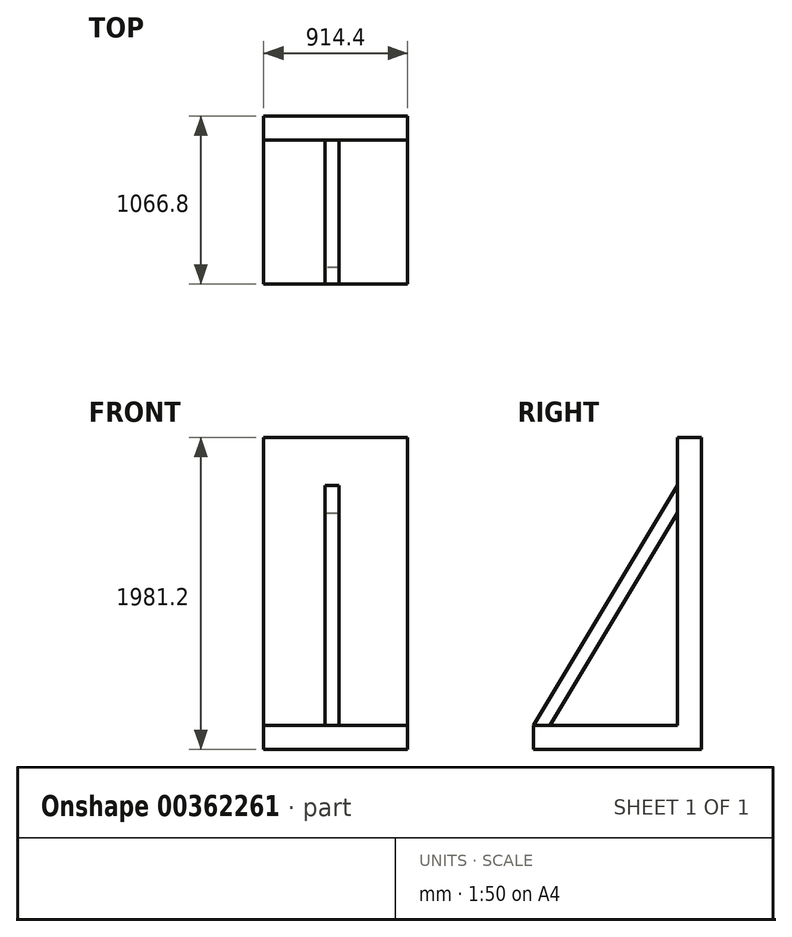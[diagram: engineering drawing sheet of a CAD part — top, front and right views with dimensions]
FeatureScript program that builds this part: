
annotation { "Feature Type Name" : "Feature", "Feature Type Description" : "" }
export const myFeature = defineFeature(function(context is Context, id is Id, definition is map)
    precondition{}
    {
        {
            var Q0;
            Q0=qCreatedBy(makeId("Front.planeOp"),FACE);
            var sketch = newSketch(context, id + "F0", { "sketchPlane" : qUnion([Q0])});
            skLineSegment(sketch, "E0.bottom", {"start": v(0, 0) * mm, "end": v(-914.4, 0) * mm});
            skLineSegment(sketch, "E0.top", {"start": v(0, 1828.8) * mm, "end": v(-914.4, 1828.8) * mm});
            skLineSegment(sketch, "E0.left", {"start": v(0, 0) * mm, "end": v(0, 1828.8) * mm});
            skLineSegment(sketch, "E0.right", {"start": v(-914.4, 0) * mm, "end": v(-914.4, 1828.8) * mm});
            skSolve(sketch);
        }
        {
            var Q0;
            Q0 = qSketchRegion(id + "F0", true);
            extrude(context, id + "F1", {"entities" : qUnion([Q0]), "depth" : 152.4 * mm});
        }
        {
            var Q0;
            Q0=qCreatedBy(makeId("Top.planeOp"),FACE);
            var sketch = newSketch(context, id + "F2", { "sketchPlane" : qUnion([Q0])});
            skLineSegment(sketch, "E1.0.0", {"start": v(0, 0) * mm, "end": v(-914.4, 0) * mm});
            skLineSegment(sketch, "E1.0.1", {"start": v(-914.4, 0) * mm, "end": v(-914.4, -152.4) * mm});
            skLineSegment(sketch, "E1.0.2", {"start": v(-914.4, -152.4) * mm, "end": v(0, -152.4) * mm});
            skLineSegment(sketch, "E1.0.3", {"start": v(0, -152.4) * mm, "end": v(0, 0) * mm});
            skLineSegment(sketch, "E2.top", {"start": v(-914.4, -1066.8) * mm, "end": v(0, -1066.8) * mm});
            skLineSegment(sketch, "E2.left", {"start": v(-914.4, -152.4) * mm, "end": v(-914.4, -1066.8) * mm});
            skLineSegment(sketch, "E2.right", {"start": v(0, -152.4) * mm, "end": v(0, -1066.8) * mm});
            skSolve(sketch);
        }
        {
            var Q0;
            Q0 = qSketchRegion(id + "F2", true);
            extrude(context, id + "F3", {"entities" : qUnion([Q0]), "operationType" : NewBodyOperationType.ADD, "oppositeDirection" : true, "depth" : 152.4 * mm});
        }
        {
            var Q0;
            Q0=makeQuery(id+"F3.opExtrude","CAP_FACE",FACE,{"disambiguationData":[OSD([sQuery(id+"F2.wireOp",EDGE,"E1.0.0"),sQuery(id+"F2.wireOp",EDGE,"E1.0.1"),sQuery(id+"F2.wireOp",EDGE,"E1.0.3"),sQuery(id+"F2.wireOp",EDGE,"E2.top"),sQuery(id+"F2.wireOp",EDGE,"E2.left"),sQuery(id+"F2.wireOp",EDGE,"E2.right")])],"isStart":true});
            var sketch = newSketch(context, id + "F4", { "sketchPlane" : qUnion([Q0])});
            skLineSegment(sketch, "E3.bottom", {"start": v(-435.57, -1066.8) * mm, "end": v(-524.47, -1066.8) * mm});
            skLineSegment(sketch, "E3.top", {"start": v(-435.57, -977.9) * mm, "end": v(-524.47, -977.9) * mm});
            skLineSegment(sketch, "E3.left", {"start": v(-435.57, -1066.8) * mm, "end": v(-435.57, -977.9) * mm});
            skLineSegment(sketch, "E3.right", {"start": v(-524.47, -1066.8) * mm, "end": v(-524.47, -977.9) * mm});
            skSolve(sketch);
        }
        {
            var Q0;
            Q0=makeQuery(id+"F1.opExtrude","CAP_FACE",FACE,{"disambiguationData":[OSD([sQuery(id+"F0.wireOp",EDGE,"E0.bottom"),sQuery(id+"F0.wireOp",EDGE,"E0.top"),sQuery(id+"F0.wireOp",EDGE,"E0.left"),sQuery(id+"F0.wireOp",EDGE,"E0.right")])],"isStart":false});
            var sketch = newSketch(context, id + "F5", { "sketchPlane" : qUnion([Q0])});
            skLineSegment(sketch, "E4", {"start": v(-457.2, 1828.8) * mm, "end": v(-457.2, 1524) * mm});
            skSolve(sketch);
        }
        {
            var Q0;
            Q0=sQuery(id+"F4.wireOp",VERTEX,"E3.right.start");
            var Q1;
            Q1=sQuery(id+"F4.wireOp",VERTEX,"E3.left.start");
            var Q2;
            Q2=sQuery(id+"F5.wireOp",VERTEX,"E4.end");
            cPlane(context, id + "F6", {"entities" : qUnion([Q0, Q1, Q2]), "cplaneType" : CPlaneType.THREE_POINT, "offset" : 25.4 * mm, "width" : 152.4 * mm, "height" : 152.4 * mm});
        }
        {
            var Q0;
            Q0=qCreatedBy(id+"F6.planeOp",FACE);
            var sketch = newSketch(context, id + "F7", { "sketchPlane" : qUnion([Q0])});
            skLineSegment(sketch, "E5.0.1", {"start": v(524.47, -548.86) * mm, "end": v(435.57, -548.86) * mm});
            skPoint(sketch, "E6.0", {"position": v(457.2, 1228.41) * mm});
            skLineSegment(sketch, "E6.1.0", {"start": v(914.4, -78.4) * mm, "end": v(0, -78.4) * mm});
            skLineSegment(sketch, "E6.1.1", {"start": v(0, -78.4) * mm, "end": v(0, 1489.77) * mm});
            skLineSegment(sketch, "E6.1.2", {"start": v(0, 1489.77) * mm, "end": v(457.2, 1489.77) * mm});
            skLineSegment(sketch, "E6.1.3", {"start": v(457.2, 1489.77) * mm, "end": v(914.4, 1489.77) * mm});
            skLineSegment(sketch, "E6.1.4", {"start": v(914.4, 1489.77) * mm, "end": v(914.4, -78.4) * mm});
            skLineSegment(sketch, "E7", {"start": v(524.47, -503.13) * mm, "end": v(524.47, 1228.41) * mm});
            skLineSegment(sketch, "E8", {"start": v(435.57, -503.13) * mm, "end": v(435.57, 1228.41) * mm});
            skLineSegment(sketch, "E9", {"start": v(435.57, 1228.41) * mm, "end": v(524.47, 1228.41) * mm});
            skLineSegment(sketch, "E10", {"start": v(524.47, -503.13) * mm, "end": v(524.47, -548.86) * mm});
            skLineSegment(sketch, "E11", {"start": v(435.57, -503.13) * mm, "end": v(435.57, -548.86) * mm});
            skSolve(sketch);
        }
        {
            var Q0;
            Q0=makeQuery(id+"F7.imprint","IMPRINT",FACE,{"disambiguationData":[TD([[makeQuery(id+"F7.imprint","IMPRINT",EDGE,{"derivedFrom":sQuery(id+"F7.wireOp",EDGE,"E5.0.1")}),-1.0]])]});
            var Q1;
            {var subQ5=sQuery(id+"F7.wireOp",EDGE,"E9");Q1=makeQuery(id+"F7.imprint","IMPRINT",FACE,{"disambiguationData":[TD([[makeQuery(id+"F7.imprint","IMPRINT",EDGE,{"derivedFrom":subQ5}),-1.0]])]});}
            extrude(context, id + "F8", {"entities" : qUnion([Q0, Q1]), "operationType" : NewBodyOperationType.ADD, "depth" : 88.9 * mm});
        }
    });
